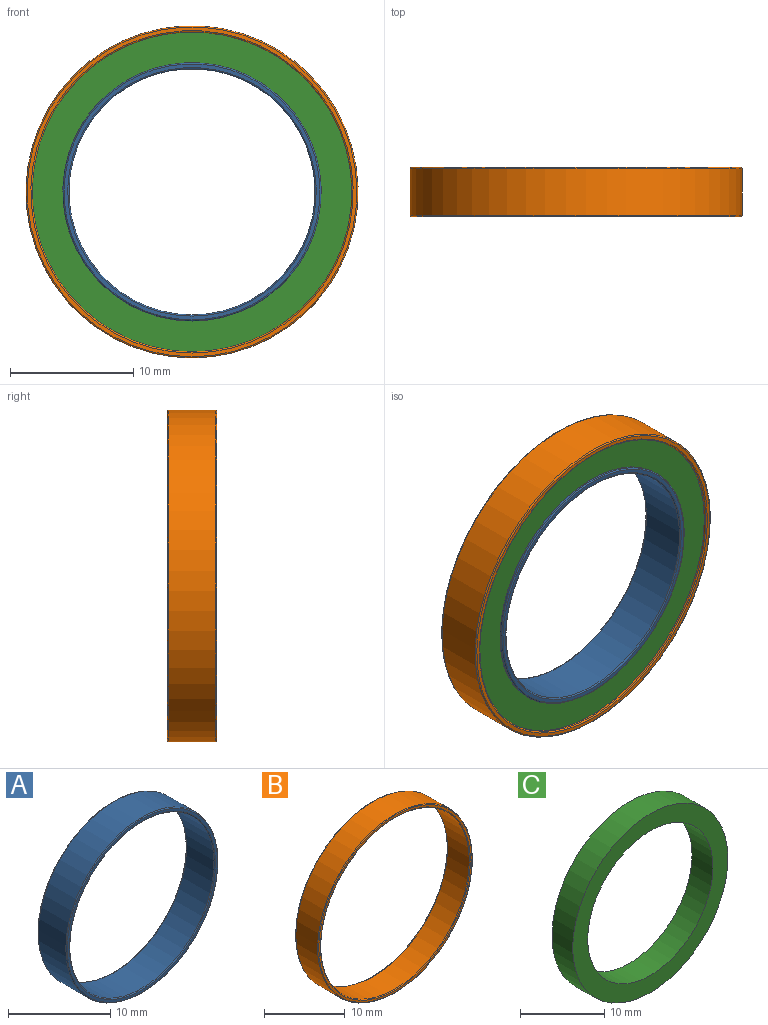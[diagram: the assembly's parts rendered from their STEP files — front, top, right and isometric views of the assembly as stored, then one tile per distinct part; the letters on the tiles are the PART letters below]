
ASSEMBLY  parts=3 mates=2
PART A: 8 faces, bbox 22.7x4x22.7 mm
  f0: cylinder r=10mm len=20mm, axis (0,1,0), area 238.8mm2, adj f4,f6
  f1: cylinder r=10.5mm len=21mm, axis (0,1,0), area 250.7mm2, adj f5,f7
  f2: plane 20.8x20.8mm, normal (0,-1,0), area 19.3mm2, adj f6,f7
  f3: plane 20.8x20.8mm, normal (0,1,0), area 19.3mm2, adj f4,f5
  f4: torus R=10.1mm, axis (0,-1,0), area 9.9mm2, adj f0,f3
  f5: torus R=10.4mm, axis (0,-1,0), area 10.3mm2, adj f1,f3
  f6: torus R=10.1mm, axis (0,-1,0), area 9.9mm2, adj f0,f2
  f7: torus R=10.4mm, axis (0,-1,0), area 10.3mm2, adj f1,f2
PART B: 8 faces, bbox 29.2x4x29.2 mm
  f0: cylinder r=13mm len=26mm, axis (0,1,0), area 310.4mm2, adj f5,f7
  f1: cylinder r=13.5mm len=27mm, axis (0,1,0), area 322.3mm2, adj f4,f6
  f2: plane 26.8x26.8mm, normal (0,-1,0), area 25mm2, adj f6,f7
  f3: plane 26.8x26.8mm, normal (0,1,0), area 25mm2, adj f4,f5
  f4: torus R=13.4mm, axis (0,-1,0), area 13.3mm2, adj f1,f3
  f5: torus R=13.1mm, axis (0,-1,0), area 12.9mm2, adj f0,f3
  f6: torus R=13.4mm, axis (0,-1,0), area 13.3mm2, adj f1,f2
  f7: torus R=13.1mm, axis (0,-1,0), area 12.9mm2, adj f0,f2
PART C: 4 faces, bbox 26x3.5x26 mm
  f0: cylinder r=10.5mm len=21mm, axis (0,1,0), area 230.9mm2, adj f2,f3
  f1: cylinder r=13mm len=26mm, axis (0,1,0), area 285.9mm2, adj f2,f3
  f2: plane 26x26mm, normal (0,-1,0), area 184.6mm2, adj f0,f1
  f3: plane 26x26mm, normal (0,1,0), area 184.6mm2, adj f0,f1
PLACE A t=(-0.3,-0.85,-1.01)mm
PLACE B t=(-0.3,-0.85,-1.01)mm
PLACE C t=(-0.3,-0.85,-1.01)mm
MATE fastened A.f0 <-> C.f0  axis (0,1,0) through (-0.3,-0.85,-1.01)mm
MATE fastened C.f0 <-> B.f0  axis (0,1,0) through (-0.3,-0.85,-1.01)mm
